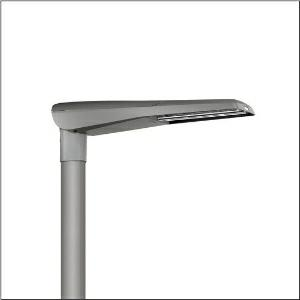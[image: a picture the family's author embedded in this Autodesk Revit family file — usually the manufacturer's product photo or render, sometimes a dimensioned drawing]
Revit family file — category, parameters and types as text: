
# Revit family: streetlight_sl_11_iq_mini___st1_2a_5xc2ac1g08he_29a3
name_source: partatom
category: Lighting Fixtures
units: mm (PartAtom-declared; Revit-internal decimal feet)

## family parameters
Cut with Voids When Loaded = No
Host = Face
Light Source = No
Part Type = Normal
Room Calculation Point = No
Round Connector Dimension = Use Diameter
Shared = No

## types (1)
- --- (1 x LED, 6820 lm, 63.6 W, 2200K)
    Apparent Load = 64 VA
    CIE Flux Codes = 32 70 96 100 100
    Color Rendering = 70
    Color Temperature = 2200K
    Default Elevation = 1800 mm
    Description = Streetlight SL 11 iQ mini, mast luminaire, primary light control with 3 zone facetted reflector, of plastic, silver coated, highly specular, primary optical cover: cover, of PMMA, transparent, light distribution: ST1.2a, light emission: direct distribution, primary light characteristic: asymmetric, installation type: post-top, side-entry, lamps: LED, High Power LED, rated values: 8.330lm | 62,2W | 133,9lm/W (begin service life); end service life: 8.330lm | 65,6W; at 50% lumin. flux: 4.165lm | 29,4W | 141,7lm/W, colour temperature: 2200/2700/3000/4000K, colour rendering: CRI > 70, light colour: 722/727/730/740, light setting 1 begin service life: 100% | 8.330lm | 62,2W | 133,9lm/W | 3.000K, light setting 1 end service life: 65,6W, further light settings possible, control: pre-setting: linear dimming characteristic, Street-Remote, Auto-Match, Temp-Guard, Lumen-Switch, Night-Set, Smart-Wire, Light-Fading, Desk-Remote (wireless, voltage-free reading and setting of iQ features in the workshop via application-optimized NFC function/RFID function), optimised constant luminous flux control (CLO 2.0), with cable H07RN-F 5x 1.5mm², mains connection: 230..240V, AC, 50/60Hz, connection cable pre-assembled, cable length: 8,5m, luminaire housing, of diecast aluminium, powder-coated, Siteco® metallic grey (DB 702S), please order mast flange separately, inclination adjustable without tools: 0°, 5°, 10°, 15° (post-top) | 0°, -5°, -10°, -15° (side-entry), sealing non-destructively replaceable, multi-level sealing system, length: 736mm, width: 174mm, height: 116mm, mast flange for spigot size: 42mm (side-entry): 5XC10008XM4, 60/48mm (side-entry/post-top): 5XC10108XM2, 76/60mm (side-entry/post-top): 5XC10108XM1, equipment: Power, protection rating (complete): IP66, insulation class (complete): insulation class II (safety insulation), certification: CE, ENEC, ENEC+, VDE, impact resistance: IK10, permissible operating ambient temperature for outdoor applications: -25..+50°C, standard-compliant lighting for roads and squares, Environmental Product Declaration (EPD) tested and certified by an independent institute, packaging unit: 1 piece

Light Distribution: ST1.2a
    Height = 116 mm
    Lamp = 1 x LED
    Lamp Light Flux = 6820 lm
    Lamp Power = 63.6 W
    Lamp count = 1
    Length = 736 mm
    Luminous efficacy = 107 lm/W
    Manufacturer = Siteco
    ModVariant = No
    Model = 5XC2AC1G08HE
    Number of Poles = 1
    OnlyDefault = Yes
    Power Factor = 1
    Product Name = Streetlight SL 11 iQ mini | ST1.2a
    Product group = mast luminaire | pylon top
    ProductGroupID = 6100
    Protection Class = Protection class II
    Protection Degree = IP 66
    RLX_Detail_Level = 1
    RLX_Emergency_Light_Flux = 0 lm
    RLX_Emergency_Type = 0
    RLX_Emergency_Type_DB = No
    RlxData = <blob elided: 53809 chars, md5=833260fd>
    Socket = socket
    Standby Power = 0 W
    System Light Flux = 6820 lm
    System Power = 64 W
    Type Comments = individual setting: luminous flux: 100 % | dim-lin: 254 | 866 mA
    Type Image = l_1003508.jpg
    URL = http://relux.com
    VarID = @adj_034594
    Voltage = 0 V
    Weight = 0.00 kg
    Width = 174 mm

## geometry (parser evidence)
native form markers: Blend x4, Sweep x11
no freeform markers — native parametric forms only
